# Revit family: Hager-Orion_Plus-IP66-D200-Cl.II-Poly_encl-630A-DE-de
name_source: partatom
category: Electrical Equipment
units: mm (PartAtom-declared; Revit-internal decimal feet)

## family parameters
Cut with Voids When Loaded = No
Host = Face
Panel Configuration = Two Columns, Circuits Across
Part Type = Panelboard
Room Calculation Point = No
Round Connector Dimension = Use Diameter
Shared = No

## types (6) — shared parameters
EF000003 - Montageart = EV000384 - Aufputz
EF000007 - Farbe = EV000270 - grau
EF000049 - Tiefe = 200 mm  [stored 0.656168 ft]
EF000116 - RAL-Nummer = 7035
EF000118 - Mit Montageplatte = No
EF000339 - Art der Abdeckung = EV004216 - Tür
EF001088 - Anbaumöglichkeit = No
EF001131 - Innentiefe = 200 mm  [stored 0.656168 ft]
EF001596 - Werkstoff des Gehäuses = EV000139 - Kunststoff
EF003532 - Geeignet für Außengebrauch = Yes
EF004464 - Art der Tür = EV002646 - Einzel
EF005474 - Schutzart (IP) = EV006422 - IP66
EF006306 - Mit Schloss = Yes
EF007800 - Geeignet für Blitzschutz = No
EF008873 - Nennstrom (In) = 630 A
EF009212 - Ausführung Deckel = EV000116 - geschlossen
EF015940 - Deckel mit Überdruckentlastung = No
HG000002 - Mit tür = Yes
HG000003 - Bereich = Orion Plus
HG000006 - Unterputz = No
HG000009 - Doppelflügeligen Tür = No
HG000010 - Asymmetrische Türen = No
HG000023 - Gehäuse mit doppeltem Querschnitt = No
HG000024 - Höhe des unteren Teils = 800 mm
HG000026 - Stehend auf dem Boden = No
Manufacturer = Hager
Type Comments = Orion Plus
zero-valued in all types: Default Elevation, EF000218 - Einbautiefe, EF000437 - Anzahl der Leitungseinführungen, EF009554 - Anzahl der Öffnungen für Flanschplatten, HG000027 - Sockelhöhe

## per-type parameters (varying)
| type | EF000008 - Breite | EF000040 - Höhe | EF000266 - Anzahl der Reihen | EF002950 - Breite in Teilungseinheiten | EF004293 - Schlagfestigkeit | EF004427 - Anzahl der Module | EF006244 - Transparenter Deckel/Tür | EF009170 - Materialstärke Gehäuse | EF009171 - Materialstärke Tür/Deckel | HG000004 - Herstellerreferenz |
| Aufputz IP66 B300 H500 T200  - FL209B | 300 mm  [stored 0.984252 ft] | 500 mm  [stored 1.64042 ft] | 3 | 12 | EV008784 - IK10 | 36 | No | 2 mm  [stored 0.00656168 ft] | 2 mm  [stored 0.00656168 ft] | FL209B |
| Aufputz IP66 B300 H500 T200  - FL259B | 300 mm  [stored 0.984252 ft] | 500 mm  [stored 1.64042 ft] | 3 | 12 | EV006814 - IK08 | 36 | Yes | 3 mm  [stored 0.00984252 ft] | 3 mm  [stored 0.00984252 ft] | FL259B |
| Aufputz IP66 B400 H500 T200  - FL213B | 400 mm  [stored 1.31234 ft] | 500 mm  [stored 1.64042 ft] | 3 | 18 | EV008784 - IK10 | 54 | No | 2 mm  [stored 0.00656168 ft] | 2 mm  [stored 0.00656168 ft] | FL213B |
| Aufputz IP66 B400 H500 T200  - FL263B | 400 mm  [stored 1.31234 ft] | 500 mm  [stored 1.64042 ft] | 3 | 18 | EV006814 - IK08 | 54 | Yes | 3 mm  [stored 0.00984252 ft] | 3 mm  [stored 0.00984252 ft] | FL263B |
| Aufputz IP66 B400 H650 T200  - FL216B | 400 mm  [stored 1.31234 ft] | 650 mm  [stored 2.13255 ft] | 4 | 18 | EV008784 - IK10 | 72 | No | 2 mm  [stored 0.00656168 ft] | 2 mm  [stored 0.00656168 ft] | FL216B |
| Aufputz IP66 B400 H650 T200  - FL266B | 400 mm  [stored 1.31234 ft] | 650 mm  [stored 2.13255 ft] | 4 | 18 | EV006814 - IK08 | 72 | Yes | 3 mm  [stored 0.00984252 ft] | 3 mm  [stored 0.00984252 ft] | FL266B |

note: [stored X ft] marks values corroborated as IEEE doubles in the binary element streams (Revit-internal decimal feet)

## geometry (parser evidence)
native form markers: Sweep x10
no freeform markers — native parametric forms only
